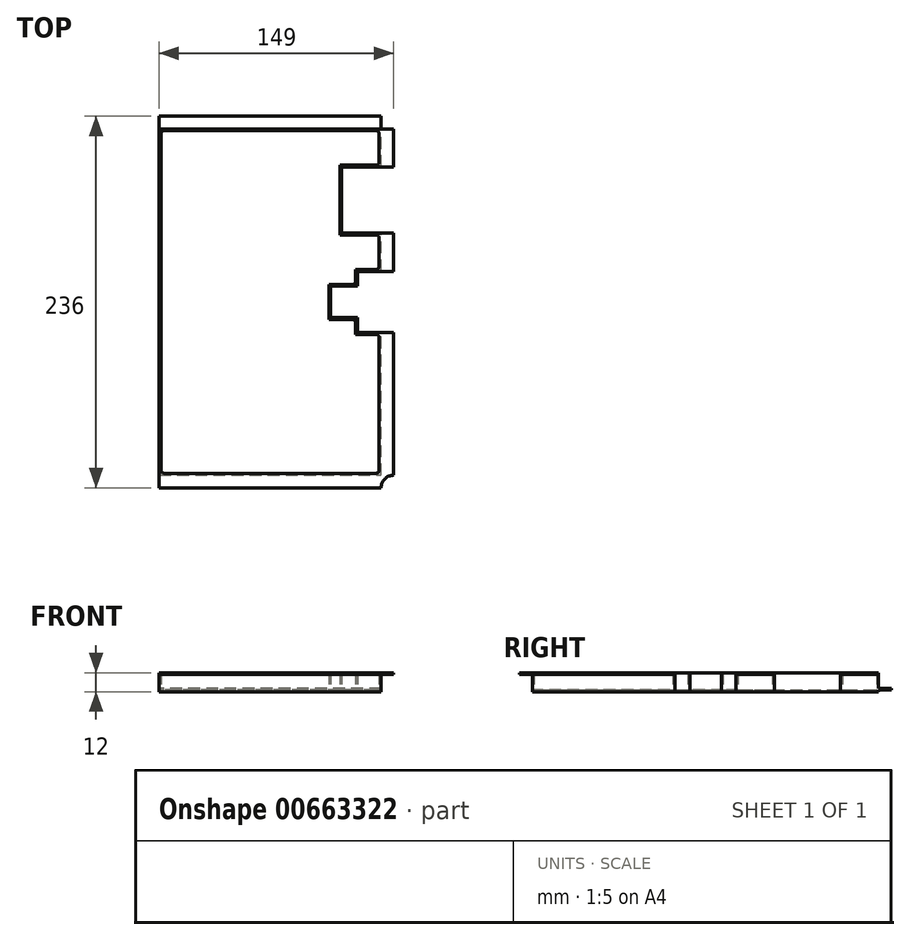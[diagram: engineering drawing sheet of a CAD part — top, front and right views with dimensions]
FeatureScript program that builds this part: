
annotation { "Feature Type Name" : "Feature", "Feature Type Description" : "" }
export const myFeature = defineFeature(function(context is Context, id is Id, definition is map)
    precondition{}
    {
        {
            var Q0;
            Q0=qCreatedBy(makeId("Top.planeOp"),FACE);
            var sketch = newSketch(context, id + "F0", { "sketchPlane" : qUnion([Q0])});
            skLineSegment(sketch, "E0.bottom", {"start": v(0, 0) * mm, "end": v(-141, 0) * mm});
            skLineSegment(sketch, "E0.top", {"start": v(0, 220) * mm, "end": v(-141, 220) * mm});
            skLineSegment(sketch, "E0.right", {"start": v(-141, 0) * mm, "end": v(-141, 220) * mm});
            skPoint(sketch, "E1", {"position": v(0, 110) * mm});
            skLineSegment(sketch, "E2", {"start": v(0, 90.5) * mm, "end": v(-15, 90.5) * mm});
            skLineSegment(sketch, "E3", {"start": v(-15, 90.5) * mm, "end": v(-15, 100) * mm});
            skLineSegment(sketch, "E4", {"start": v(-15, 100) * mm, "end": v(-32, 100) * mm});
            skLineSegment(sketch, "E5", {"start": v(0, 110) * mm, "end": v(-32, 110) * mm, "construction": true});
            skLineSegment(sketch, "E6.MirrorCS", {"start": v(0, 129.5) * mm, "end": v(-15, 129.5) * mm});
            skLineSegment(sketch, "E7.MirrorCS", {"start": v(-15, 120) * mm, "end": v(-32, 120) * mm});
            skLineSegment(sketch, "E8.MirrorCS", {"start": v(-15, 129.5) * mm, "end": v(-15, 120) * mm});
            skLineSegment(sketch, "E9", {"start": v(-32, 120) * mm, "end": v(-32, 100) * mm});
            skLineSegment(sketch, "E10", {"start": v(0, 90.5) * mm, "end": v(0, 0) * mm});
            skLineSegment(sketch, "E11", {"start": v(0, 129.5) * mm, "end": v(0, 220) * mm, "construction": true});
            skPoint(sketch, "E12", {"position": v(-141, 110) * mm});
            skPoint(sketch, "E13", {"position": v(25.78, 174.75) * mm});
            skPoint(sketch, "E14", {"position": v(0, 174.75) * mm});
            skLineSegment(sketch, "E15", {"start": v(0, 174.75) * mm, "end": v(-25, 174.75) * mm, "construction": true});
            skLineSegment(sketch, "E16", {"start": v(0, 129.5) * mm, "end": v(0, 153.75) * mm});
            skLineSegment(sketch, "E17", {"start": v(0, 153.75) * mm, "end": v(-25, 153.75) * mm});
            skLineSegment(sketch, "E18", {"start": v(-25, 153.75) * mm, "end": v(-25, 174.75) * mm});
            skLineSegment(sketch, "E19.MirrorCS", {"start": v(0, 195.75) * mm, "end": v(-25, 195.75) * mm});
            skLineSegment(sketch, "E20.MirrorCS", {"start": v(-25, 195.75) * mm, "end": v(-25, 174.75) * mm});
            skLineSegment(sketch, "E21", {"start": v(0, 195.75) * mm, "end": v(0, 220) * mm});
            skLineSegment(sketch, "E22.0", {"start": v(-1.2, 196.95) * mm, "end": v(-26.2, 196.95) * mm});
            skLineSegment(sketch, "E22.1", {"start": v(-26.2, 196.95) * mm, "end": v(-26.2, 174.75) * mm});
            skLineSegment(sketch, "E22.2", {"start": v(-26.2, 152.55) * mm, "end": v(-26.2, 174.75) * mm});
            skLineSegment(sketch, "E22.3", {"start": v(-1.2, 152.55) * mm, "end": v(-26.2, 152.55) * mm});
            skLineSegment(sketch, "E22.4", {"start": v(-1.2, 130.7) * mm, "end": v(-1.2, 152.55) * mm});
            skLineSegment(sketch, "E22.5", {"start": v(-1.2, 196.95) * mm, "end": v(-1.2, 218.8) * mm});
            skLineSegment(sketch, "E22.6", {"start": v(-1.2, 130.7) * mm, "end": v(-16.2, 130.7) * mm});
            skLineSegment(sketch, "E22.7", {"start": v(-1.2, 89.3) * mm, "end": v(-1.2, 1.2) * mm});
            skLineSegment(sketch, "E22.8", {"start": v(-1.2, 1.2) * mm, "end": v(-139.8, 1.2) * mm});
            skLineSegment(sketch, "E22.9", {"start": v(-139.8, 1.2) * mm, "end": v(-139.8, 218.8) * mm});
            skLineSegment(sketch, "E22.10", {"start": v(-1.2, 218.8) * mm, "end": v(-139.8, 218.8) * mm});
            skLineSegment(sketch, "E22.11", {"start": v(-1.2, 89.3) * mm, "end": v(-16.2, 89.3) * mm});
            skLineSegment(sketch, "E22.12", {"start": v(-16.2, 89.3) * mm, "end": v(-16.2, 98.8) * mm});
            skLineSegment(sketch, "E22.13", {"start": v(-16.2, 98.8) * mm, "end": v(-33.2, 98.8) * mm});
            skLineSegment(sketch, "E22.14", {"start": v(-33.2, 121.2) * mm, "end": v(-33.2, 98.8) * mm});
            skLineSegment(sketch, "E22.15", {"start": v(-16.2, 121.2) * mm, "end": v(-33.2, 121.2) * mm});
            skLineSegment(sketch, "E22.16", {"start": v(-16.2, 130.7) * mm, "end": v(-16.2, 121.2) * mm});
            skSolve(sketch);
        }
        {
            var Q0;
            Q0 = qSketchRegion(id + "F0", true);
            extrude(context, id + "F1", {"entities" : qUnion([Q0]), "flatOperationType" : FlatOperationType.REMOVE, "depth" : 12 * mm, "offsetDistance" : 25 * mm, "domain" : OperationDomain.MODEL});
        }
        {
            var Q0;
            Q0=makeQuery(id+"F0.imprint","IMPRINT",FACE,{"disambiguationData":[TD([[makeQuery(id+"F0.imprint","IMPRINT",EDGE,{"derivedFrom":sQuery(id+"F0.wireOp",EDGE,"E22.0")}),-1.0]])]});
            extrude(context, id + "F2", {"entities" : qUnion([Q0]), "operationType" : NewBodyOperationType.ADD, "flatOperationType" : FlatOperationType.REMOVE, "depth" : 1 * mm, "offsetDistance" : 25 * mm, "domain" : OperationDomain.MODEL});
        }
        {
            var Q0;
            Q0=makeQuery(id+"F1.opExtrude","SWEPT_FACE",FACE,{"disambiguationData":[OSD([sQuery(id+"F0.wireOp",EDGE,"E0.bottom")])]});
            var sketch = newSketch(context, id + "F3", { "sketchPlane" : qUnion([Q0])});
            skLineSegment(sketch, "E23.bottom", {"start": v(-141, 12) * mm, "end": v(0, 12) * mm});
            skLineSegment(sketch, "E23.top", {"start": v(-141, 11) * mm, "end": v(0, 11) * mm});
            skLineSegment(sketch, "E23.left", {"start": v(-141, 12) * mm, "end": v(-141, 11) * mm});
            skLineSegment(sketch, "E23.right", {"start": v(0, 12) * mm, "end": v(0, 11) * mm});
            skSolve(sketch);
        }
        {
            var Q0;
            Q0 = qSketchRegion(id + "F3", true);
            extrude(context, id + "F4", {"entities" : qUnion([Q0]), "operationType" : NewBodyOperationType.ADD, "depth" : 8 * mm, "offsetDistance" : 25 * mm});
        }
        {
            var Q0;
            Q0=makeQuery(id+"F4.boolean.opBoolean","MERGE",FACE,{"derivedFrom":[makeQuery(id+"F1.opExtrude","SWEPT_FACE",FACE,{"disambiguationData":[OSD([sQuery(id+"F0.wireOp",EDGE,"E10")])]}),makeQuery(id+"F4.opExtrude","SWEPT_FACE",FACE,{"disambiguationData":[OSD([sQuery(id+"F3.wireOp",EDGE,"E23.right")])]})]});
            var sketch = newSketch(context, id + "F5", { "sketchPlane" : qUnion([Q0])});
            skLineSegment(sketch, "E24.bottom", {"start": v(0, 11) * mm, "end": v(90.5, 11) * mm});
            skLineSegment(sketch, "E24.top", {"start": v(0, 12) * mm, "end": v(90.5, 12) * mm});
            skLineSegment(sketch, "E24.left", {"start": v(0, 11) * mm, "end": v(0, 12) * mm});
            skLineSegment(sketch, "E24.right", {"start": v(90.5, 11) * mm, "end": v(90.5, 12) * mm});
            skSolve(sketch);
        }
        {
            var Q0;
            Q0 = qSketchRegion(id + "F5", true);
            extrude(context, id + "F6", {"entities" : qUnion([Q0]), "operationType" : NewBodyOperationType.ADD, "depth" : 8 * mm, "offsetDistance" : 25 * mm});
        }
        {
            var Q0;
            Q0=makeQuery(id+"F1.opExtrude","SWEPT_FACE",FACE,{"disambiguationData":[OSD([sQuery(id+"F0.wireOp",EDGE,"E16")])]});
            var sketch = newSketch(context, id + "F7", { "sketchPlane" : qUnion([Q0])});
            skLineSegment(sketch, "E25.bottom", {"start": v(129.5, 12) * mm, "end": v(153.75, 12) * mm});
            skLineSegment(sketch, "E25.top", {"start": v(129.5, 11) * mm, "end": v(153.75, 11) * mm});
            skLineSegment(sketch, "E25.left", {"start": v(129.5, 12) * mm, "end": v(129.5, 11) * mm});
            skLineSegment(sketch, "E25.right", {"start": v(153.75, 12) * mm, "end": v(153.75, 11) * mm});
            skSolve(sketch);
        }
        {
            var Q0;
            Q0 = qSketchRegion(id + "F7", true);
            extrude(context, id + "F8", {"entities" : qUnion([Q0]), "operationType" : NewBodyOperationType.ADD, "depth" : 8 * mm, "offsetDistance" : 25 * mm});
        }
        {
            var Q0;
            Q0=makeQuery(id+"F1.opExtrude","SWEPT_FACE",FACE,{"disambiguationData":[OSD([sQuery(id+"F0.wireOp",EDGE,"E21")])]});
            var sketch = newSketch(context, id + "F9", { "sketchPlane" : qUnion([Q0])});
            skLineSegment(sketch, "E26.bottom", {"start": v(195.75, 12) * mm, "end": v(220, 12) * mm});
            skLineSegment(sketch, "E26.top", {"start": v(195.75, 11) * mm, "end": v(220, 11) * mm});
            skLineSegment(sketch, "E26.left", {"start": v(195.75, 12) * mm, "end": v(195.75, 11) * mm});
            skLineSegment(sketch, "E26.right", {"start": v(220, 12) * mm, "end": v(220, 11) * mm});
            skSolve(sketch);
        }
        {
            var Q0;
            Q0 = qSketchRegion(id + "F9", true);
            extrude(context, id + "F10", {"entities" : qUnion([Q0]), "operationType" : NewBodyOperationType.ADD, "depth" : 8 * mm, "offsetDistance" : 25 * mm});
        }
        {
            var Q0;
            Q0=makeQuery(id+"F10.boolean.opBoolean","MERGE",FACE,{"derivedFrom":[makeQuery(id+"F1.opExtrude","SWEPT_FACE",FACE,{"disambiguationData":[OSD([sQuery(id+"F0.wireOp",EDGE,"E0.top")])]}),makeQuery(id+"F10.opExtrude","SWEPT_FACE",FACE,{"disambiguationData":[OSD([sQuery(id+"F9.wireOp",EDGE,"E26.right")])]})]});
            var sketch = newSketch(context, id + "F11", { "sketchPlane" : qUnion([Q0])});
            skLineSegment(sketch, "E27.bottom", {"start": v(0, 1.2) * mm, "end": v(141, 1.2) * mm});
            skLineSegment(sketch, "E27.top", {"start": v(0, 2.2) * mm, "end": v(141, 2.2) * mm});
            skLineSegment(sketch, "E27.left", {"start": v(0, 1.2) * mm, "end": v(0, 2.2) * mm});
            skLineSegment(sketch, "E27.right", {"start": v(141, 1.2) * mm, "end": v(141, 2.2) * mm});
            skSolve(sketch);
        }
        {
            var Q0;
            Q0 = qSketchRegion(id + "F11", true);
            extrude(context, id + "F12", {"entities" : qUnion([Q0]), "operationType" : NewBodyOperationType.ADD, "depth" : 8 * mm, "offsetDistance" : 25 * mm});
        }
        {
            var Q0;
            Q0=makeQuery(id+"F6.opExtrude","CAP_EDGE",EDGE,{"disambiguationData":[OSD([sQuery(id+"F5.wireOp",EDGE,"E24.left")])],"isStart":true});
            fillet(context, id + "F13", {"entities" : qUnion([Q0]), "radius" : 8 * mm, "tangentPropagation" : true, "allowEdgeOverflow" : false});
        }
        {
            var Q0;
            Q0=makeQuery(id+"F1.opExtrude","SWEPT_EDGE",EDGE,{"disambiguationData":[OSD([sQuery(id+"F0.wireOp",EDGE,"E22.9"),sQuery(id+"F0.wireOp",EDGE,"E22.10")])]});
            var Q1;
            Q1=makeQuery(id+"F1.opExtrude","SWEPT_EDGE",EDGE,{"disambiguationData":[OSD([sQuery(id+"F0.wireOp",EDGE,"E22.3"),sQuery(id+"F0.wireOp",EDGE,"E22.4")])]});
            var Q2;
            Q2=makeQuery(id+"F1.opExtrude","SWEPT_EDGE",EDGE,{"disambiguationData":[OSD([sQuery(id+"F0.wireOp",EDGE,"E22.5"),sQuery(id+"F0.wireOp",EDGE,"E22.10")])]});
            var Q3;
            Q3=makeQuery(id+"F1.opExtrude","SWEPT_EDGE",EDGE,{"disambiguationData":[OSD([sQuery(id+"F0.wireOp",EDGE,"E22.0"),sQuery(id+"F0.wireOp",EDGE,"E22.5")])]});
            var Q4;
            Q4=makeQuery(id+"F1.opExtrude","SWEPT_EDGE",EDGE,{"disambiguationData":[OSD([sQuery(id+"F0.wireOp",EDGE,"E22.4"),sQuery(id+"F0.wireOp",EDGE,"E22.6")])]});
            var Q5;
            Q5=makeQuery(id+"F1.opExtrude","SWEPT_EDGE",EDGE,{"disambiguationData":[OSD([sQuery(id+"F0.wireOp",EDGE,"E22.15"),sQuery(id+"F0.wireOp",EDGE,"E22.16")])]});
            var Q6;
            Q6=makeQuery(id+"F1.opExtrude","SWEPT_EDGE",EDGE,{"disambiguationData":[OSD([sQuery(id+"F0.wireOp",EDGE,"E22.12"),sQuery(id+"F0.wireOp",EDGE,"E22.13")])]});
            var Q7;
            Q7=makeQuery(id+"F1.opExtrude","SWEPT_EDGE",EDGE,{"disambiguationData":[OSD([sQuery(id+"F0.wireOp",EDGE,"E22.7"),sQuery(id+"F0.wireOp",EDGE,"E22.11")])]});
            var Q8;
            Q8=makeQuery(id+"F1.opExtrude","SWEPT_EDGE",EDGE,{"disambiguationData":[OSD([sQuery(id+"F0.wireOp",EDGE,"E22.7"),sQuery(id+"F0.wireOp",EDGE,"E22.8")])]});
            var Q9;
            Q9=makeQuery(id+"F1.opExtrude","SWEPT_EDGE",EDGE,{"disambiguationData":[OSD([sQuery(id+"F0.wireOp",EDGE,"E22.8"),sQuery(id+"F0.wireOp",EDGE,"E22.9")])]});
            fillet(context, id + "F14", {"entities" : qUnion([Q0, Q1, Q2, Q3, Q4, Q5, Q6, Q7, Q8, Q9]), "radius" : 2 * mm, "tangentPropagation" : true, "allowEdgeOverflow" : false});
        }
    });
